# Revit family: Gira_039201
name_source: partatom
category: Electrical Fixtures
revit_build: Autodesk Revit 2017 (Build: 20160225_1515(x64)
units: mm (PartAtom-declared; Revit-internal decimal feet)

## family parameters
Cut with Voids When Loaded = No
Host = Face
Maintain Annotation Orientation = Yes
Part Type = Normal
Room Calculation Point = No
Round Connector Dimension = Use Diameter
Shared = No

## types (1)
- RTC 230 V  NC con. 1-way + ctrl.l. System 55 cr.white
    Adjustable differential = No
    Available = No
    BIM (1) = https://media.stage.bim.site und Tasten.rfa?public/gira/36a6b08/Sys55_Komplettgerät_Schalten und Tasten.rfa
    Category = Room thermostat
    Connection = Two-wire
    Control characteristic = Other
    Cooling = No
    Data sheet (1) = https://katalog.gira.de
    Default Elevation = 1219 mm
    Description = RTC 230V NC con.1-w ctrl.l. Sys55 CW,Room temperature controller 230 10 (4) A~  with NC contact, 1-way switch and control light,System 55,cream white glossy,Notes :,- For screw mounting only.,- Flat design.
    Explosion-proof = No
    External sensor = No
    GTIN = 4010337392019
    HAN = 039201
    Heating = Yes
    HeinzeBIM = https://bimportal.heinze.de
    Manufacturer = Gira
    Manufacturer URL = https://www.gira.de
    Measuring range maximum value = 30
    Measuring range minimum value = 5
    Model = On/Off
    Name = RTC 230 V  NC con. 1-way + ctrl.l. System 55 cr.white
    RAL-number = 1013
    Sensor/feeler type = Other
    Temperature readable = No
    Thermal feedback = None
    URL = http://katalog.gira.de
    With receiver = No
    With sound indicator = No
    With tap water circuit = No

## geometry (parser evidence)
native form markers: Blend x2, Sweep x11
no freeform markers — native parametric forms only
